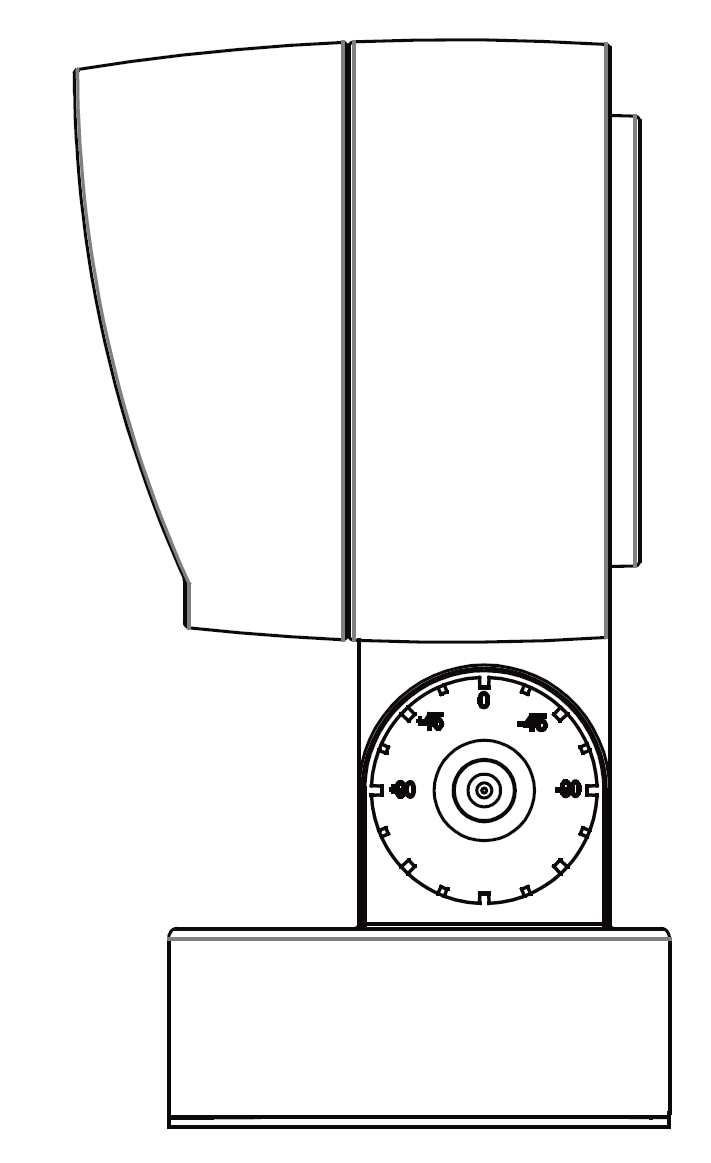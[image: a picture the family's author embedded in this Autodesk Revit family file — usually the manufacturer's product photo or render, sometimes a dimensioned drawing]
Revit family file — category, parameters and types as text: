
# Revit family: Holly Flood Light_26W_3000K
name_source: partatom
category: Lighting Fixtures
units: mm (PartAtom-declared; Revit-internal decimal feet)

## family parameters
Always vertical = Yes
Cut with Voids When Loaded = No
Light Source = No
Maintain Annotation Orientation = No
Part Type = Normal
Room Calculation Point = No
Round Connector Dimension = Use Diameter
Shared = No
Work Plane-Based = No

## types (5) — shared parameters
Assembly Code = HOLLY Flood Light - Canopy Cover
CCT = 3000K
CRI = 80
Default Elevation = 0' - 0"
Height = 0' - 8 13/32"
IP Rating = 65
Input Voltage = 120-277V
Lamp = LED
Load Classification = Lighting
Manufacturer = Above All Lighting
Power Factor = 0.9
URL = https://www.abovealllighting.com
Wattage Comments = 26W
Width = 0' - 5 1/8"

## per-type parameters (varying)
| type | Beam Angle | Delivered Lumen | Light Source | Model |
| Holly Flood _26w_3000K_5° | 5.00° | 1320 lx | 26W-Tiltable : Holly Flood_26W_3000K_5° | HOFL_C26301_5 |
| Holly Flood _26w_3000K_15° | 15.00° | 2200 lx | 26W-Tiltable : Holly Flood_26W_3000K_15° | HOFL_C26301_15 |
| Holly Flood _26w_3000K_24° | 24.00° | 2200 lx | 26W-Tiltable : Holly Flood_26W_3000K_24° | HOFL_C26301_24 |
| Holly Flood _26w_3000K_36° | 36.00° | 2200 lx | 26W-Tiltable : Holly Flood_26W_3000K_36° | HOFL_C26301_36 |
| Holly Flood _26w_3000K_50° | 50.00° | 2200 lx | 26W-Tiltable : Holly Flood_26W_3000K_50° | HOFL_C26301_50 |

## geometry (parser evidence)
native form markers: Sweep x9
no freeform markers — native parametric forms only
